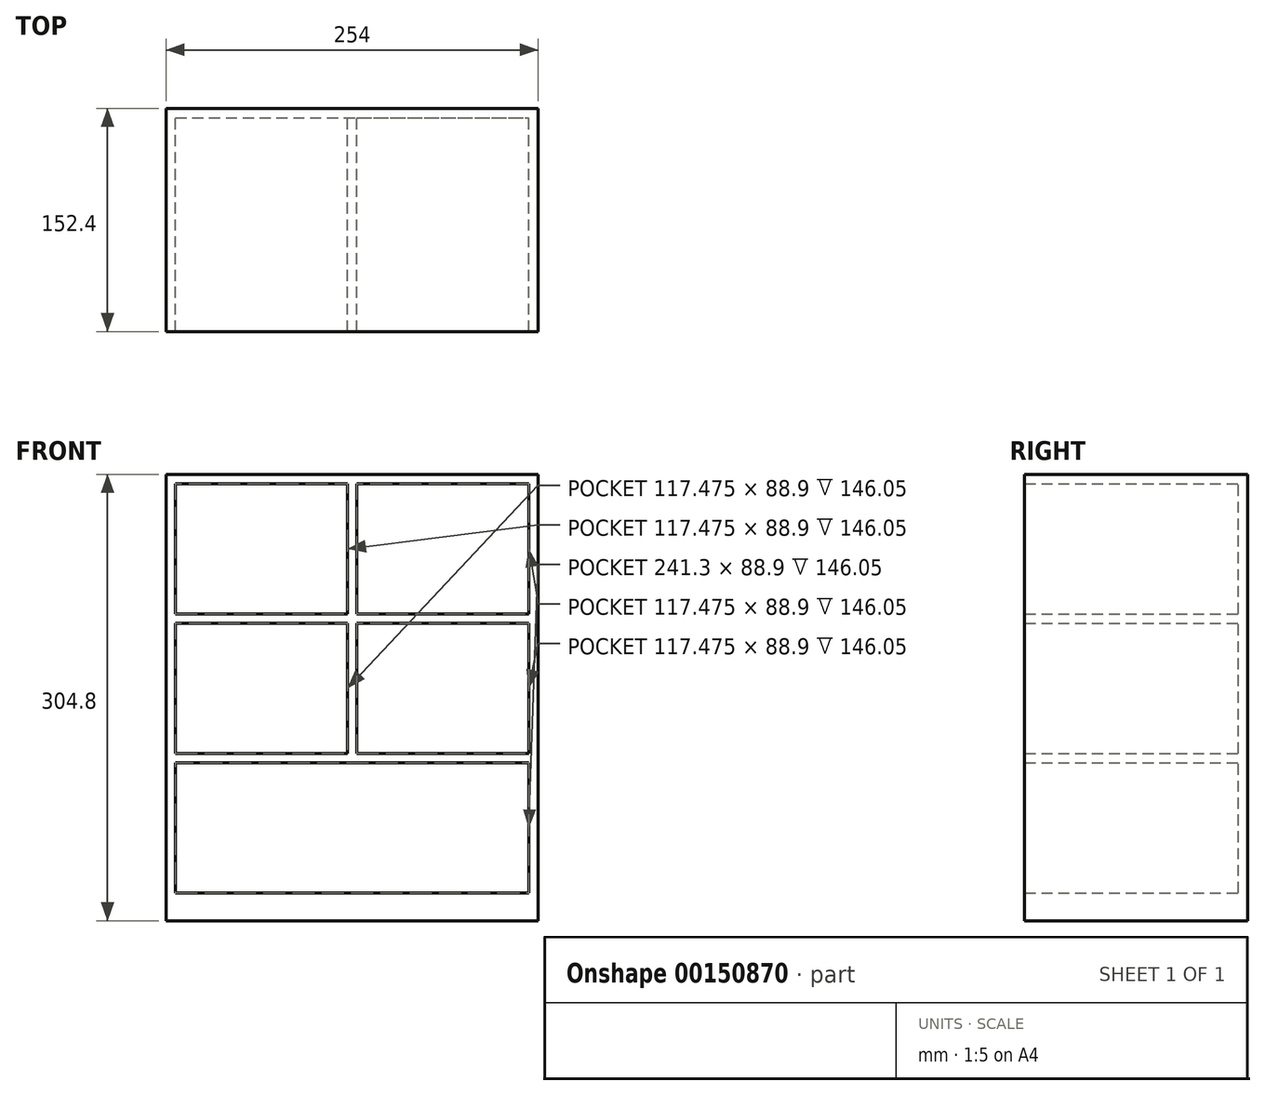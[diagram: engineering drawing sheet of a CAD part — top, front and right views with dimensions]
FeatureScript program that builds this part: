
annotation { "Feature Type Name" : "Feature", "Feature Type Description" : "" }
export const myFeature = defineFeature(function(context is Context, id is Id, definition is map)
    precondition{}
    {
        {
            var Q0;
            Q0=qCreatedBy(makeId("Front.planeOp"),FACE);
            var sketch = newSketch(context, id + "F0", { "sketchPlane" : qUnion([Q0])});
            skLineSegment(sketch, "E0.bottom", {"start": v(0, 0) * mm, "end": v(254, 0) * mm});
            skLineSegment(sketch, "E0.top", {"start": v(0, 304.8) * mm, "end": v(254, 304.8) * mm});
            skLineSegment(sketch, "E0.left", {"start": v(0, 0) * mm, "end": v(0, 304.8) * mm});
            skLineSegment(sketch, "E0.right", {"start": v(254, 0) * mm, "end": v(254, 304.8) * mm});
            skLineSegment(sketch, "E1.bottom", {"start": v(6.35, 19.05) * mm, "end": v(247.65, 19.05) * mm});
            skLineSegment(sketch, "E1.left", {"start": v(6.35, 19.05) * mm, "end": v(6.35, 107.95) * mm});
            skLineSegment(sketch, "E2.bottom", {"start": v(6.35, 298.45) * mm, "end": v(123.82, 298.45) * mm});
            skLineSegment(sketch, "E2.top", {"start": v(6.35, 209.55) * mm, "end": v(123.82, 209.55) * mm});
            skLineSegment(sketch, "E2.left", {"start": v(6.35, 298.45) * mm, "end": v(6.35, 209.55) * mm});
            skLineSegment(sketch, "E2.right", {"start": v(123.82, 298.45) * mm, "end": v(123.82, 209.55) * mm});
            skLineSegment(sketch, "E3", {"start": v(6.35, 107.95) * mm, "end": v(247.65, 107.95) * mm});
            skLineSegment(sketch, "E4", {"start": v(247.65, 19.05) * mm, "end": v(247.65, 107.95) * mm});
            skLineSegment(sketch, "E5.bottom", {"start": v(6.35, 114.3) * mm, "end": v(123.82, 114.3) * mm});
            skLineSegment(sketch, "E5.top", {"start": v(6.35, 203.2) * mm, "end": v(123.82, 203.2) * mm});
            skLineSegment(sketch, "E5.left", {"start": v(6.35, 114.3) * mm, "end": v(6.35, 203.2) * mm});
            skLineSegment(sketch, "E5.right", {"start": v(123.82, 114.3) * mm, "end": v(123.82, 203.2) * mm});
            skLineSegment(sketch, "E6.bottom", {"start": v(130.17, 114.3) * mm, "end": v(247.65, 114.3) * mm});
            skLineSegment(sketch, "E6.top", {"start": v(130.17, 203.2) * mm, "end": v(247.65, 203.2) * mm});
            skLineSegment(sketch, "E6.left", {"start": v(130.17, 114.3) * mm, "end": v(130.17, 203.2) * mm});
            skLineSegment(sketch, "E6.right", {"start": v(247.65, 114.3) * mm, "end": v(247.65, 203.2) * mm});
            skLineSegment(sketch, "E7.bottom", {"start": v(130.17, 209.55) * mm, "end": v(247.65, 209.55) * mm});
            skLineSegment(sketch, "E7.top", {"start": v(130.17, 298.45) * mm, "end": v(247.65, 298.45) * mm});
            skLineSegment(sketch, "E7.left", {"start": v(130.17, 209.55) * mm, "end": v(130.17, 298.45) * mm});
            skLineSegment(sketch, "E7.right", {"start": v(247.65, 209.55) * mm, "end": v(247.65, 298.45) * mm});
            skSolve(sketch);
        }
        {
            var Q0;
            Q0 = qSketchRegion(id + "F0", true);
            extrude(context, id + "F1", {"entities" : qUnion([Q0]), "depth" : 152.4 * mm});
        }
        {
            var Q0;
            Q0=qCreatedBy(makeId("Front.planeOp"),FACE);
            var sketch = newSketch(context, id + "F2", { "sketchPlane" : qUnion([Q0])});
            skLineSegment(sketch, "E8.bottom", {"start": v(0, 0) * mm, "end": v(254, 0) * mm});
            skLineSegment(sketch, "E8.top", {"start": v(0, 304.8) * mm, "end": v(254, 304.8) * mm});
            skLineSegment(sketch, "E8.left", {"start": v(0, 0) * mm, "end": v(0, 304.8) * mm});
            skLineSegment(sketch, "E8.right", {"start": v(254, 0) * mm, "end": v(254, 304.8) * mm});
            skSolve(sketch);
        }
        {
            var Q0;
            Q0 = qSketchRegion(id + "F2", true);
            extrude(context, id + "F3", {"entities" : qUnion([Q0]), "operationType" : NewBodyOperationType.ADD, "depth" : 6.35 * mm});
        }
    });
